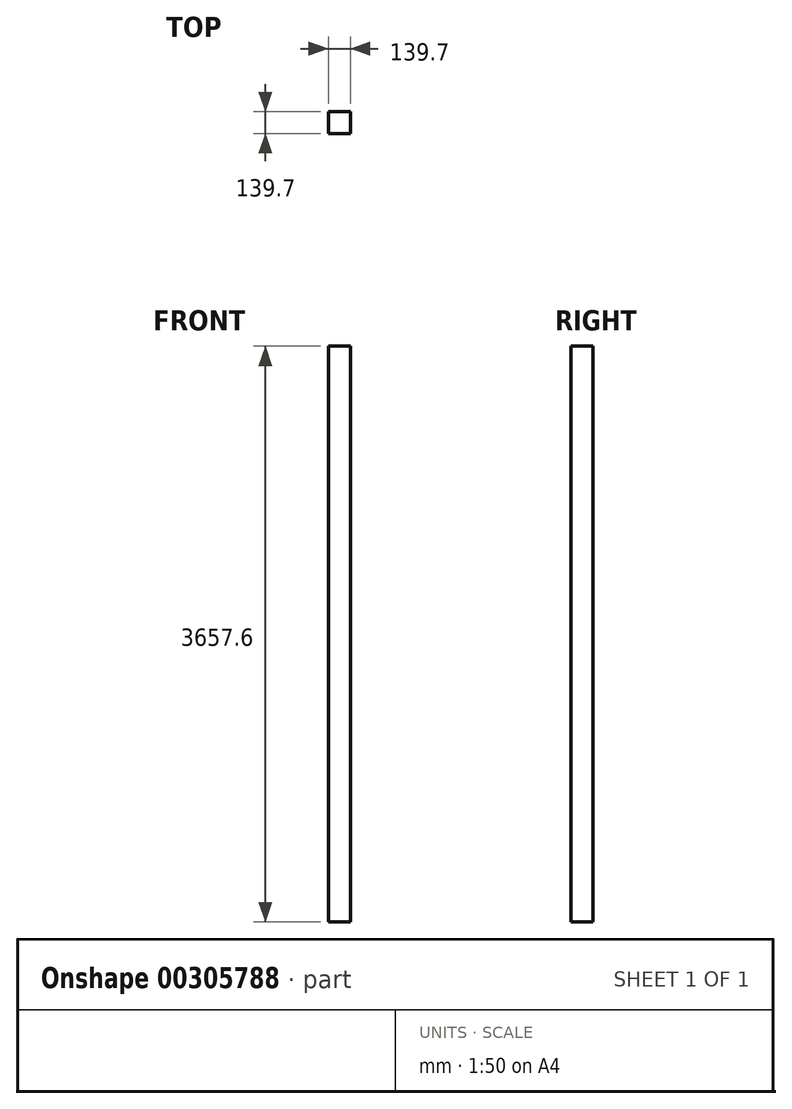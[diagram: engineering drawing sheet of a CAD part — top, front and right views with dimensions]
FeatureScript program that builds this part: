
annotation { "Feature Type Name" : "Feature", "Feature Type Description" : "" }
export const myFeature = defineFeature(function(context is Context, id is Id, definition is map)
    precondition{}
    {
        {
            var Q0;
            Q0=qCreatedBy(makeId("Top.planeOp"),FACE);
            var sketch = newSketch(context, id + "F0", { "sketchPlane" : qUnion([Q0])});
            skLineSegment(sketch, "E0.bottom", {"start": v(0, 0) * mm, "end": v(139.7, 0) * mm});
            skLineSegment(sketch, "E0.top", {"start": v(0, 139.7) * mm, "end": v(139.7, 139.7) * mm});
            skLineSegment(sketch, "E0.left", {"start": v(0, 0) * mm, "end": v(0, 139.7) * mm});
            skLineSegment(sketch, "E0.right", {"start": v(139.7, 0) * mm, "end": v(139.7, 139.7) * mm});
            skSolve(sketch);
        }
        {
            var Q0;
            Q0=qSketchRegion(id+"F0",true);
            extrude(context, id + "F1", {"entities" : qUnion([Q0]), "depth" : 3657.6 * mm});
        }
    });
